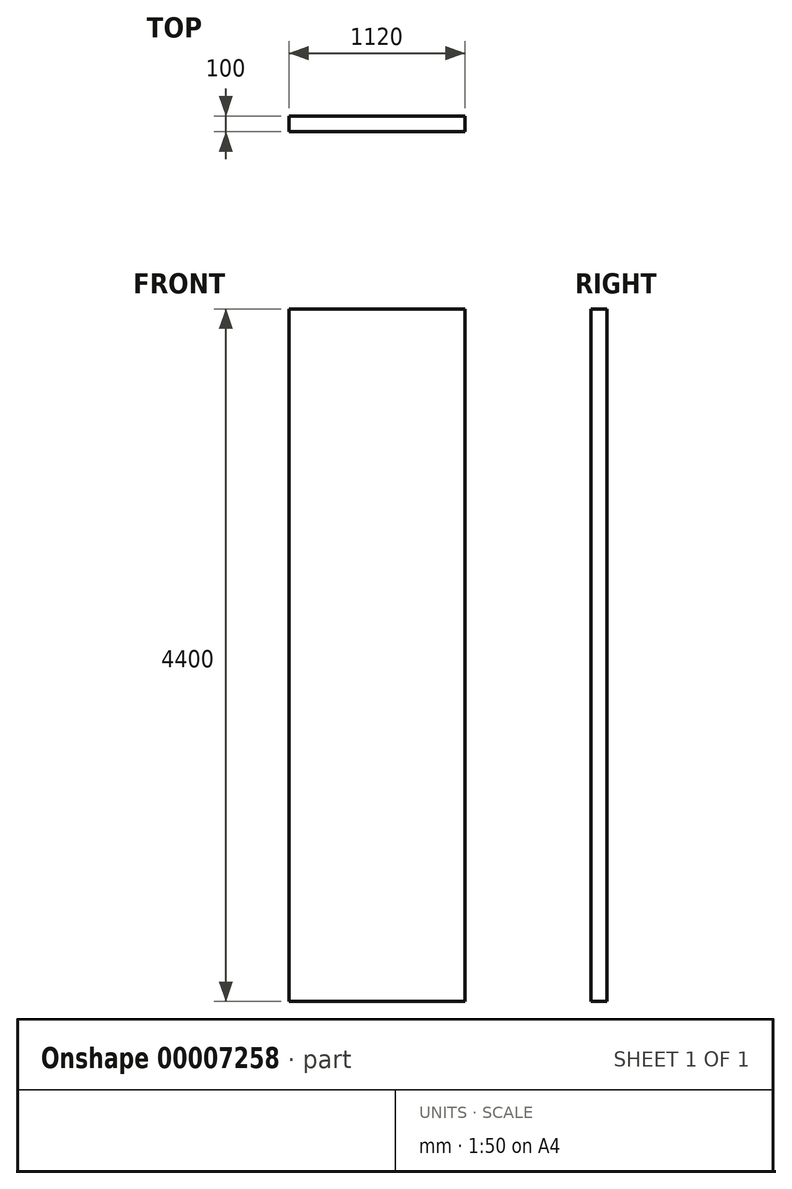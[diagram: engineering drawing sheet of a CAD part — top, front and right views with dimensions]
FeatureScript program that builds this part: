
annotation { "Feature Type Name" : "Feature", "Feature Type Description" : "" }
export const myFeature = defineFeature(function(context is Context, id is Id, definition is map)
    precondition{}
    {
        {
            var Q0;
            Q0=qCreatedBy(makeId("Front.planeOp"),FACE);
            var sketch = newSketch(context, id + "F0", { "sketchPlane" : qUnion([Q0])});
            skLineSegment(sketch, "E0", {"start": v(0, 0) * mm, "end": v(1120, 0) * mm});
            skLineSegment(sketch, "E1", {"start": v(1120, 0) * mm, "end": v(1120, 4400) * mm});
            skLineSegment(sketch, "E2", {"start": v(1120, 4400) * mm, "end": v(0, 4400) * mm});
            skLineSegment(sketch, "E3", {"start": v(0, 4400) * mm, "end": v(0, 0) * mm});
            skSolve(sketch);
        }
        {
            var Q0;
            Q0=makeQuery(id+"F0.imprint","IMPRINT",FACE,{"disambiguationData":[TD([[makeQuery(id+"F0.imprint","IMPRINT",EDGE,{"derivedFrom":sQuery(id+"F0.wireOp",EDGE,"E0")}),1.0]])]});
            extrude(context, id + "F1", {"entities" : qUnion([Q0]), "depth" : 100 * mm});
        }
    });
